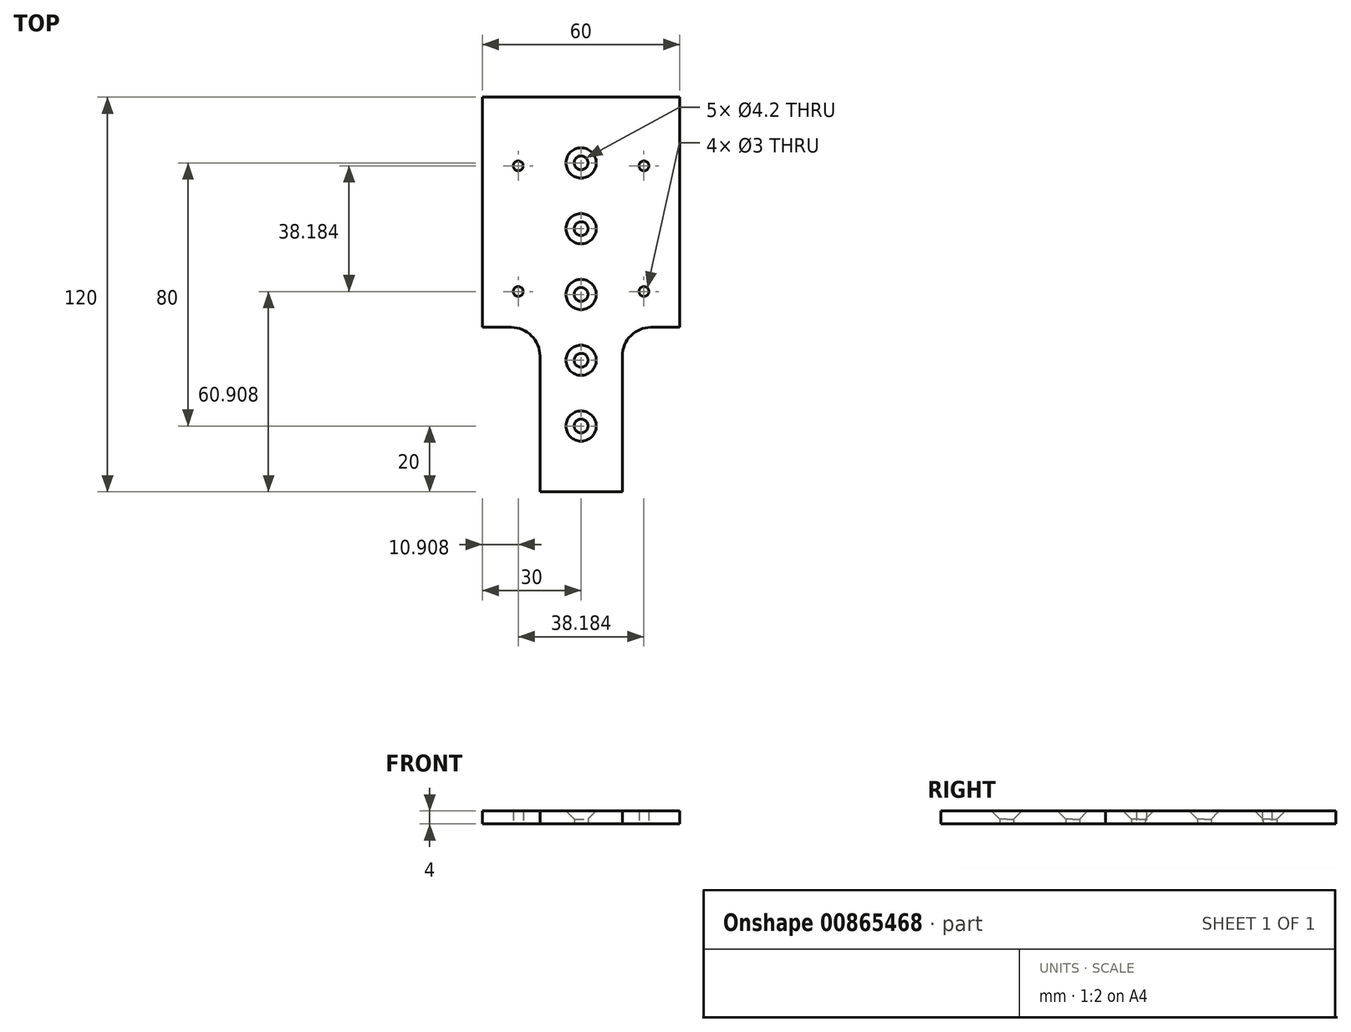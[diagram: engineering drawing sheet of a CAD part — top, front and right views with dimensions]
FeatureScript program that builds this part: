
annotation { "Feature Type Name" : "Feature", "Feature Type Description" : "" }
export const myFeature = defineFeature(function(context is Context, id is Id, definition is map)
    precondition{}
    {
        {
            var Q0;
            Q0=qCreatedBy(makeId("Top.planeOp"),FACE);
            var sketch = newSketch(context, id + "F0", { "sketchPlane" : qUnion([Q0])});
            skLineSegment(sketch, "E0.bottom", {"start": v(30, 80) * mm, "end": v(-30, 80) * mm});
            skLineSegment(sketch, "E0.top", {"start": v(30, -80) * mm, "end": v(-30, -80) * mm});
            skLineSegment(sketch, "E0.left", {"start": v(30, 80) * mm, "end": v(30, -80) * mm});
            skLineSegment(sketch, "E0.right", {"start": v(-30, 80) * mm, "end": v(-30, -80) * mm});
            skPoint(sketch, "E0.middle", {"position": v(0, 0) * mm});
            skCircle(sketch, "E1", {"center": v(0, 0) * mm, "radius": 27 * mm});
            skLineSegment(sketch, "E2", {"start": v(0, 0) * mm, "end": v(-19.1, 19.1) * mm});
            skLineSegment(sketch, "E3", {"start": v(0, 0) * mm, "end": v(19.1, -19.1) * mm});
            skLineSegment(sketch, "E4", {"start": v(0, 0) * mm, "end": v(19.1, 19.1) * mm});
            skLineSegment(sketch, "E5", {"start": v(0, 0) * mm, "end": v(-19.1, -19.1) * mm});
            skCircle(sketch, "E6", {"center": v(-19.1, 19.1) * mm, "radius": 1.5 * mm});
            skCircle(sketch, "E7", {"center": v(19.1, 19.1) * mm, "radius": 1.5 * mm});
            skCircle(sketch, "E8", {"center": v(19.1, -19.1) * mm, "radius": 1.5 * mm});
            skCircle(sketch, "E9", {"center": v(-19.1, -19.1) * mm, "radius": 1.5 * mm});
            skPoint(sketch, "E10.center.orphan", {"position": v(-20, -70) * mm});
            skPoint(sketch, "E11.center.orphan", {"position": v(20, -70) * mm});
            skSolve(sketch);
        }
        {
            var Q0;
            Q0 = qSketchRegion(id + "F0", true);
            var Q1;
            {var subQ0=sQuery(id+"F0.wireOp",EDGE,"E6");var subQ1=sQuery(id+"F0.wireOp",EDGE,"E1");var subQ2=makeQuery(id+"F0.imprint","INTERSECT",VERTEX,{"disambiguationData":[OD(1.0)],"derivedFrom":[subQ1,subQ0]});Q1=makeQuery(id+"F0.imprint","IMPRINT",FACE,{"disambiguationData":[TD([[makeQuery(id+"F0.imprint","IMPRINT",EDGE,{"disambiguationData":[TD([[subQ2,-1.0]])],"derivedFrom":subQ1}),1.0]])]});}
            var Q2;
            {var subQ3=sQuery(id+"F0.wireOp",EDGE,"E7");var subQ6=sQuery(id+"F0.wireOp",EDGE,"E1");var subQ9=makeQuery(id+"F0.imprint","INTERSECT",VERTEX,{"disambiguationData":[OD(1.0)],"derivedFrom":[subQ6,subQ3]});Q2=makeQuery(id+"F0.imprint","IMPRINT",FACE,{"disambiguationData":[TD([[makeQuery(id+"F0.imprint","IMPRINT",EDGE,{"disambiguationData":[TD([[subQ9,-1.0]])],"derivedFrom":subQ6}),1.0]])]});}
            var Q3;
            {var subQ0=sQuery(id+"F0.wireOp",EDGE,"E7");var subQ1=sQuery(id+"F0.wireOp",EDGE,"E1");var subQ2=makeQuery(id+"F0.imprint","INTERSECT",VERTEX,{"disambiguationData":[OD(0.0)],"derivedFrom":[subQ1,subQ0]});Q3=makeQuery(id+"F0.imprint","IMPRINT",FACE,{"disambiguationData":[TD([[makeQuery(id+"F0.imprint","IMPRINT",EDGE,{"disambiguationData":[TD([[subQ2,1.0]])],"derivedFrom":subQ1}),1.0]])]});}
            var Q4;
            {var subQ1=sQuery(id+"F0.wireOp",EDGE,"E1");var subQ7=sQuery(id+"F0.wireOp",EDGE,"E9");var subQ9=makeQuery(id+"F0.imprint","INTERSECT",VERTEX,{"disambiguationData":[OD(1.0)],"derivedFrom":[subQ1,subQ7]});Q4=makeQuery(id+"F0.imprint","IMPRINT",FACE,{"disambiguationData":[TD([[makeQuery(id+"F0.imprint","IMPRINT",EDGE,{"disambiguationData":[TD([[subQ9,-1.0]])],"derivedFrom":subQ1}),1.0]])]});}
            extrude(context, id + "F1", {"entities" : qUnion([Q0, Q1, Q2, Q3, Q4]), "depth" : 4 * mm, "offsetDistance" : 25 * mm});
        }
        {
            var Q0;
            Q0=makeQuery(id+"F1.opExtrude","CAP_FACE",FACE,{"disambiguationData":[OSD([sQuery(id+"F0.wireOp",EDGE,"E0.bottom"),sQuery(id+"F0.wireOp",EDGE,"E0.top"),sQuery(id+"F0.wireOp",EDGE,"E0.left"),sQuery(id+"F0.wireOp",EDGE,"E0.right"),sQuery(id+"F0.wireOp",EDGE,"E6"),sQuery(id+"F0.wireOp",EDGE,"E7"),sQuery(id+"F0.wireOp",EDGE,"E8"),sQuery(id+"F0.wireOp",EDGE,"E9"),sQuery(id+"F0.wireOp",EDGE,"E10"),sQuery(id+"F0.wireOp",EDGE,"E11")])],"isStart":false});
            var sketch = newSketch(context, id + "F2", { "sketchPlane" : qUnion([Q0])});
            skLineSegment(sketch, "E12.bottom", {"start": v(-30, 80) * mm, "end": v(30, 80) * mm});
            skLineSegment(sketch, "E12.top", {"start": v(-30, 40) * mm, "end": v(30, 40) * mm});
            skLineSegment(sketch, "E12.left", {"start": v(-30, 80) * mm, "end": v(-30, 40) * mm});
            skLineSegment(sketch, "E12.right", {"start": v(30, 80) * mm, "end": v(30, 40) * mm});
            skSolve(sketch);
        }
        {
            var Q0;
            Q0 = qSketchRegion(id + "F2", true);
            extrude(context, id + "F3", {"entities" : qUnion([Q0]), "operationType" : NewBodyOperationType.REMOVE, "endBound" : BoundingType.THROUGH_ALL, "oppositeDirection" : true, "depth" : 25 * mm, "offsetDistance" : 25 * mm});
        }
        {
            var Q0;
            Q0=makeQuery(id+"F1.opExtrude","CAP_FACE",FACE,{"disambiguationData":[OSD([sQuery(id+"F0.wireOp",EDGE,"E0.bottom"),sQuery(id+"F0.wireOp",EDGE,"E0.top"),sQuery(id+"F0.wireOp",EDGE,"E0.left"),sQuery(id+"F0.wireOp",EDGE,"E0.right"),sQuery(id+"F0.wireOp",EDGE,"E6"),sQuery(id+"F0.wireOp",EDGE,"E7"),sQuery(id+"F0.wireOp",EDGE,"E8"),sQuery(id+"F0.wireOp",EDGE,"E9"),sQuery(id+"F0.wireOp",EDGE,"E10"),sQuery(id+"F0.wireOp",EDGE,"E11")])],"isStart":true});
            var sketch = newSketch(context, id + "F4", { "sketchPlane" : qUnion([Q0])});
            skCircle(sketch, "E13", {"center": v(0, 40) * mm, "radius": 2.1 * mm});
            skCircle(sketch, "E14", {"center": v(0, 0) * mm, "radius": 2.1 * mm});
            skCircle(sketch, "E15", {"center": v(0, 20) * mm, "radius": 2.1 * mm});
            skCircle(sketch, "E16", {"center": v(0, -20) * mm, "radius": 2.1 * mm});
            skCircle(sketch, "E17", {"center": v(0, 60) * mm, "radius": 2.1 * mm});
            skSolve(sketch);
        }
        {
            var Q0;
            Q0 = qSketchRegion(id + "F4", true);
            extrude(context, id + "F5", {"entities" : qUnion([Q0]), "operationType" : NewBodyOperationType.REMOVE, "endBound" : BoundingType.THROUGH_ALL, "oppositeDirection" : true, "depth" : 25 * mm, "offsetDistance" : 25 * mm});
        }
        {
            var Q0;
            Q0=makeQuery(id+"F5.boolean.opBoolean","INTERSECT",EDGE,{"derivedFrom":[makeQuery(id+"F1.opExtrude","CAP_FACE",FACE,{"disambiguationData":[OSD([sQuery(id+"F0.wireOp",EDGE,"E0.bottom"),sQuery(id+"F0.wireOp",EDGE,"E0.top"),sQuery(id+"F0.wireOp",EDGE,"E0.left"),sQuery(id+"F0.wireOp",EDGE,"E0.right"),sQuery(id+"F0.wireOp",EDGE,"E6"),sQuery(id+"F0.wireOp",EDGE,"E7"),sQuery(id+"F0.wireOp",EDGE,"E8"),sQuery(id+"F0.wireOp",EDGE,"E9")])],"isStart":false}),makeQuery(id+"F5.opExtrude","SWEPT_FACE",FACE,{"disambiguationData":[OSD([sQuery(id+"F4.wireOp",EDGE,"E17")])]})]});
            var Q1;
            Q1=makeQuery(id+"F5.boolean.opBoolean","INTERSECT",EDGE,{"derivedFrom":[makeQuery(id+"F1.opExtrude","CAP_FACE",FACE,{"disambiguationData":[OSD([sQuery(id+"F0.wireOp",EDGE,"E0.bottom"),sQuery(id+"F0.wireOp",EDGE,"E0.top"),sQuery(id+"F0.wireOp",EDGE,"E0.left"),sQuery(id+"F0.wireOp",EDGE,"E0.right"),sQuery(id+"F0.wireOp",EDGE,"E6"),sQuery(id+"F0.wireOp",EDGE,"E7"),sQuery(id+"F0.wireOp",EDGE,"E8"),sQuery(id+"F0.wireOp",EDGE,"E9")])],"isStart":false}),makeQuery(id+"F5.opExtrude","SWEPT_FACE",FACE,{"disambiguationData":[OSD([sQuery(id+"F4.wireOp",EDGE,"E13")])]})]});
            var Q2;
            Q2=makeQuery(id+"F5.boolean.opBoolean","INTERSECT",EDGE,{"derivedFrom":[makeQuery(id+"F1.opExtrude","CAP_FACE",FACE,{"disambiguationData":[OSD([sQuery(id+"F0.wireOp",EDGE,"E0.bottom"),sQuery(id+"F0.wireOp",EDGE,"E0.top"),sQuery(id+"F0.wireOp",EDGE,"E0.left"),sQuery(id+"F0.wireOp",EDGE,"E0.right"),sQuery(id+"F0.wireOp",EDGE,"E6"),sQuery(id+"F0.wireOp",EDGE,"E7"),sQuery(id+"F0.wireOp",EDGE,"E8"),sQuery(id+"F0.wireOp",EDGE,"E9")])],"isStart":false}),makeQuery(id+"F5.opExtrude","SWEPT_FACE",FACE,{"disambiguationData":[OSD([sQuery(id+"F4.wireOp",EDGE,"E15")])]})]});
            var Q3;
            Q3=makeQuery(id+"F5.boolean.opBoolean","INTERSECT",EDGE,{"derivedFrom":[makeQuery(id+"F1.opExtrude","CAP_FACE",FACE,{"disambiguationData":[OSD([sQuery(id+"F0.wireOp",EDGE,"E0.bottom"),sQuery(id+"F0.wireOp",EDGE,"E0.top"),sQuery(id+"F0.wireOp",EDGE,"E0.left"),sQuery(id+"F0.wireOp",EDGE,"E0.right"),sQuery(id+"F0.wireOp",EDGE,"E6"),sQuery(id+"F0.wireOp",EDGE,"E7"),sQuery(id+"F0.wireOp",EDGE,"E8"),sQuery(id+"F0.wireOp",EDGE,"E9")])],"isStart":false}),makeQuery(id+"F5.opExtrude","SWEPT_FACE",FACE,{"disambiguationData":[OSD([sQuery(id+"F4.wireOp",EDGE,"E14")])]})]});
            var Q4;
            Q4=makeQuery(id+"F5.boolean.opBoolean","INTERSECT",EDGE,{"derivedFrom":[makeQuery(id+"F1.opExtrude","CAP_FACE",FACE,{"disambiguationData":[OSD([sQuery(id+"F0.wireOp",EDGE,"E0.bottom"),sQuery(id+"F0.wireOp",EDGE,"E0.top"),sQuery(id+"F0.wireOp",EDGE,"E0.left"),sQuery(id+"F0.wireOp",EDGE,"E0.right"),sQuery(id+"F0.wireOp",EDGE,"E6"),sQuery(id+"F0.wireOp",EDGE,"E7"),sQuery(id+"F0.wireOp",EDGE,"E8"),sQuery(id+"F0.wireOp",EDGE,"E9")])],"isStart":false}),makeQuery(id+"F5.opExtrude","SWEPT_FACE",FACE,{"disambiguationData":[OSD([sQuery(id+"F4.wireOp",EDGE,"E16")])]})]});
            chamfer(context, id + "F6", {"entities" : qUnion([Q0, Q1, Q2, Q3, Q4]), "width" : 2.5 * mm, "tangentPropagation" : true});
        }
        {
            var Q0;
            Q0=makeQuery(id+"F1.opExtrude","CAP_FACE",FACE,{"disambiguationData":[OSD([sQuery(id+"F0.wireOp",EDGE,"E0.bottom"),sQuery(id+"F0.wireOp",EDGE,"E0.top"),sQuery(id+"F0.wireOp",EDGE,"E0.left"),sQuery(id+"F0.wireOp",EDGE,"E0.right"),sQuery(id+"F0.wireOp",EDGE,"E6"),sQuery(id+"F0.wireOp",EDGE,"E7"),sQuery(id+"F0.wireOp",EDGE,"E8"),sQuery(id+"F0.wireOp",EDGE,"E9")])],"isStart":true});
            var sketch = newSketch(context, id + "F7", { "sketchPlane" : qUnion([Q0])});
            skLineSegment(sketch, "E18.bottom", {"start": v(-30, 80) * mm, "end": v(-12.5, 80) * mm});
            skLineSegment(sketch, "E18.top", {"start": v(-30, 30) * mm, "end": v(-12.5, 30) * mm});
            skLineSegment(sketch, "E18.left", {"start": v(-30, 80) * mm, "end": v(-30, 30) * mm});
            skLineSegment(sketch, "E18.right", {"start": v(-12.5, 80) * mm, "end": v(-12.5, 30) * mm});
            skLineSegment(sketch, "E19.bottom", {"start": v(30, 80) * mm, "end": v(12.5, 80) * mm});
            skLineSegment(sketch, "E19.top", {"start": v(30, 30) * mm, "end": v(12.5, 30) * mm});
            skLineSegment(sketch, "E19.left", {"start": v(30, 80) * mm, "end": v(30, 30) * mm});
            skLineSegment(sketch, "E19.right", {"start": v(12.5, 80) * mm, "end": v(12.5, 30) * mm});
            skSolve(sketch);
        }
        {
            var Q0;
            Q0 = qSketchRegion(id + "F7", true);
            extrude(context, id + "F8", {"entities" : qUnion([Q0]), "operationType" : NewBodyOperationType.REMOVE, "endBound" : BoundingType.THROUGH_ALL, "oppositeDirection" : true, "depth" : 25 * mm, "offsetDistance" : 25 * mm});
        }
        {
            var Q0;
            Q0=makeQuery(id+"F8.boolean.opBoolean","COPY",EDGE,{"derivedFrom":makeQuery(id+"F8.opExtrude","SWEPT_EDGE",EDGE,{"disambiguationData":[OSD([sQuery(id+"F7.wireOp",EDGE,"E18.top"),sQuery(id+"F7.wireOp",EDGE,"E18.right")])]})});
            var Q1;
            Q1=makeQuery(id+"F8.boolean.opBoolean","COPY",EDGE,{"derivedFrom":makeQuery(id+"F8.opExtrude","SWEPT_EDGE",EDGE,{"disambiguationData":[OSD([sQuery(id+"F0.wireOp",EDGE,"E0.right"),sQuery(id+"F7.wireOp",EDGE,"E18.top"),sQuery(id+"F7.wireOp",EDGE,"E18.left")])]})});
            var Q2;
            Q2=makeQuery(id+"F8.boolean.opBoolean","COPY",EDGE,{"derivedFrom":makeQuery(id+"F8.opExtrude","SWEPT_EDGE",EDGE,{"disambiguationData":[OSD([sQuery(id+"F7.wireOp",EDGE,"E19.top"),sQuery(id+"F7.wireOp",EDGE,"E19.right")])]})});
            var Q3;
            Q3=makeQuery(id+"F8.boolean.opBoolean","COPY",EDGE,{"derivedFrom":makeQuery(id+"F8.opExtrude","SWEPT_EDGE",EDGE,{"disambiguationData":[OSD([sQuery(id+"F0.wireOp",EDGE,"E0.left"),sQuery(id+"F7.wireOp",EDGE,"E19.top"),sQuery(id+"F7.wireOp",EDGE,"E19.left")])]})});
            var Q4;
            Q4=makeQuery(id+"F3.boolean.opBoolean","COPY",EDGE,{"derivedFrom":makeQuery(id+"F3.opExtrude","SWEPT_EDGE",EDGE,{"disambiguationData":[OSD([sQuery(id+"F0.wireOp",EDGE,"E0.right"),sQuery(id+"F2.wireOp",EDGE,"E12.top"),sQuery(id+"F2.wireOp",EDGE,"E12.left")])]})});
            var Q5;
            Q5=makeQuery(id+"F3.boolean.opBoolean","COPY",EDGE,{"derivedFrom":makeQuery(id+"F3.opExtrude","SWEPT_EDGE",EDGE,{"disambiguationData":[OSD([sQuery(id+"F0.wireOp",EDGE,"E0.left"),sQuery(id+"F2.wireOp",EDGE,"E12.top"),sQuery(id+"F2.wireOp",EDGE,"E12.right")])]})});
            var Q6;
            Q6=makeQuery(id+"F8.boolean.opBoolean","COPY",EDGE,{"derivedFrom":makeQuery(id+"F8.opExtrude","SWEPT_EDGE",EDGE,{"disambiguationData":[OSD([sQuery(id+"F0.wireOp",EDGE,"E0.top"),sQuery(id+"F7.wireOp",EDGE,"E18.bottom"),sQuery(id+"F7.wireOp",EDGE,"E18.right")])]})});
            var Q7;
            Q7=makeQuery(id+"F8.boolean.opBoolean","COPY",EDGE,{"derivedFrom":makeQuery(id+"F8.opExtrude","SWEPT_EDGE",EDGE,{"disambiguationData":[OSD([sQuery(id+"F0.wireOp",EDGE,"E0.top"),sQuery(id+"F7.wireOp",EDGE,"E19.bottom"),sQuery(id+"F7.wireOp",EDGE,"E19.right")])]})});
            fillet(context, id + "F9", {"entities" : qUnion([Q0, Q1, Q2, Q3, Q4, Q5, Q6, Q7]), "radius" : 8.75 * mm, "tangentPropagation" : true, "allowEdgeOverflow" : false});
        }
    });
